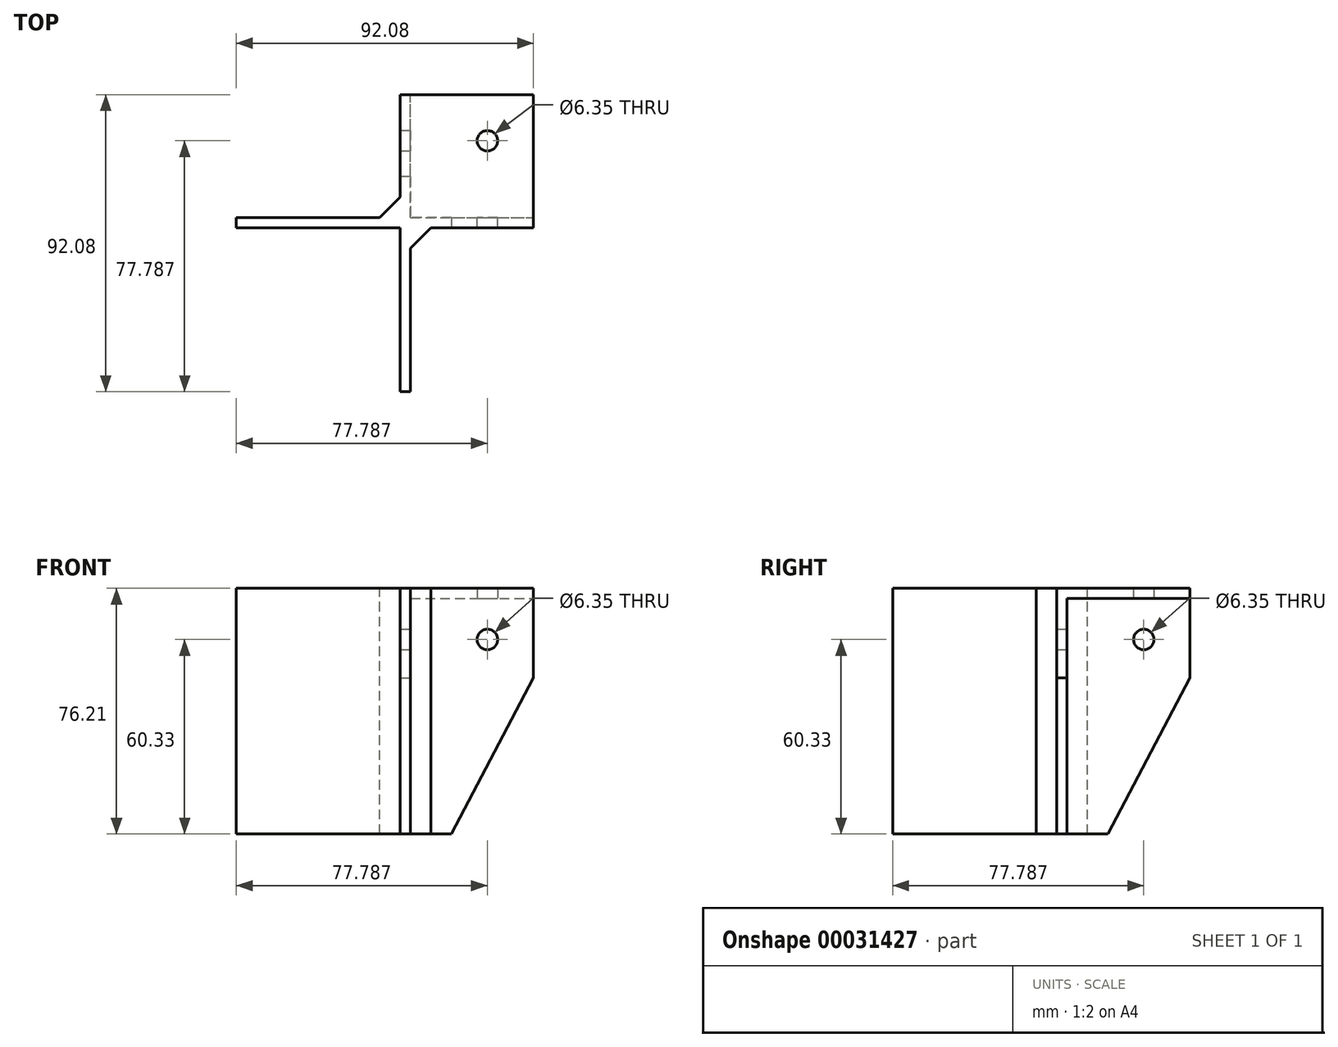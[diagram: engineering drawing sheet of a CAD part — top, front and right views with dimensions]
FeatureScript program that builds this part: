
annotation { "Feature Type Name" : "Feature", "Feature Type Description" : "" }
export const myFeature = defineFeature(function(context is Context, id is Id, definition is map)
    precondition{}
    {
        {
            var Q0;
            Q0=qCreatedBy(makeId("Top.planeOp"),FACE);
            var sketch = newSketch(context, id + "F0", { "sketchPlane" : qUnion([Q0])});
            skLineSegment(sketch, "E0.bottom", {"start": v(0, 0) * mm, "end": v(50.8, 0) * mm});
            skLineSegment(sketch, "E0.top", {"start": v(0, 50.8) * mm, "end": v(50.8, 50.8) * mm});
            skLineSegment(sketch, "E0.left", {"start": v(0, 0) * mm, "end": v(0, 50.8) * mm});
            skLineSegment(sketch, "E0.right", {"start": v(50.8, 0) * mm, "end": v(50.8, 50.8) * mm});
            skSolve(sketch);
        }
        {
            var Q0;
            Q0=makeQuery(id+"F0.imprint","IMPRINT",FACE,{"disambiguationData":[TD([[makeQuery(id+"F0.imprint","IMPRINT",EDGE,{"derivedFrom":sQuery(id+"F0.wireOp",EDGE,"E0.bottom")}),1.0]])]});
            extrude(context, id + "F1", {"entities" : qUnion([Q0]), "depth" : 3.17 * mm});
        }
        {
            var Q0;
            Q0=makeQuery(id+"F1.opExtrude","CAP_FACE",FACE,{"disambiguationData":[OSD([sQuery(id+"F0.wireOp",EDGE,"E0.bottom"),sQuery(id+"F0.wireOp",EDGE,"E0.top"),sQuery(id+"F0.wireOp",EDGE,"E0.left"),sQuery(id+"F0.wireOp",EDGE,"E0.right")])],"isStart":false});
            var sketch = newSketch(context, id + "F2", { "sketchPlane" : qUnion([Q0])});
            skLineSegment(sketch, "E1.bottom", {"start": v(50.8, 0) * mm, "end": v(-50.8, 0) * mm});
            skLineSegment(sketch, "E1.top", {"start": v(50.8, 3.18) * mm, "end": v(-50.8, 3.18) * mm});
            skLineSegment(sketch, "E1.left", {"start": v(50.8, 0) * mm, "end": v(50.8, 3.18) * mm});
            skLineSegment(sketch, "E1.right", {"start": v(-50.8, 0) * mm, "end": v(-50.8, 3.18) * mm});
            skSolve(sketch);
        }
        {
            var Q0;
            {var subQ5=sQuery(id+"F2.wireOp",EDGE,"E1.right");Q0=makeQuery(id+"F2.imprint","IMPRINT",FACE,{"disambiguationData":[TD([[makeQuery(id+"F2.imprint","IMPRINT",EDGE,{"derivedFrom":subQ5}),-1.0]])]});}
            var Q1;
            {var subQ5=sQuery(id+"F2.wireOp",EDGE,"E1.left");Q1=makeQuery(id+"F2.imprint","IMPRINT",FACE,{"disambiguationData":[TD([[makeQuery(id+"F2.imprint","IMPRINT",EDGE,{"derivedFrom":subQ5}),1.0]])]});}
            extrude(context, id + "F3", {"entities" : qUnion([Q0, Q1]), "operationType" : NewBodyOperationType.ADD, "depth" : 12.7 * mm, "hasSecondDirection" : true, "secondDirectionOppositeDirection" : true, "secondDirectionDepth" : 76.2 * mm});
        }
        {
            var Q0;
            Q0=makeQuery(id+"F1.opExtrude","CAP_FACE",FACE,{"disambiguationData":[OSD([sQuery(id+"F0.wireOp",EDGE,"E0.bottom"),sQuery(id+"F0.wireOp",EDGE,"E0.top"),sQuery(id+"F0.wireOp",EDGE,"E0.left"),sQuery(id+"F0.wireOp",EDGE,"E0.right")])],"isStart":false});
            var sketch = newSketch(context, id + "F4", { "sketchPlane" : qUnion([Q0])});
            skLineSegment(sketch, "E2.bottom", {"start": v(0, 50.8) * mm, "end": v(3.18, 50.8) * mm});
            skLineSegment(sketch, "E2.top", {"start": v(0, -50.8) * mm, "end": v(3.18, -50.8) * mm});
            skLineSegment(sketch, "E2.left", {"start": v(0, 50.8) * mm, "end": v(0, -50.8) * mm});
            skLineSegment(sketch, "E2.right", {"start": v(3.18, 50.8) * mm, "end": v(3.18, -50.8) * mm});
            skSolve(sketch);
        }
        {
            var Q0;
            Q0 = qSketchRegion(id + "F4", true);
            extrude(context, id + "F5", {"entities" : qUnion([Q0]), "operationType" : NewBodyOperationType.ADD, "depth" : 12.7 * mm, "hasSecondDirection" : true, "secondDirectionOppositeDirection" : true, "secondDirectionDepth" : 76.2 * mm});
        }
        {
            var Q0;
            Q0=makeQuery(id+"F5.boolean.opBoolean","MERGE",FACE,{"derivedFrom":[makeQuery(id+"F3.opExtrude","CAP_FACE",FACE,{"disambiguationData":[OSD([sQuery(id+"F2.wireOp",EDGE,"E1.bottom"),sQuery(id+"F2.wireOp",EDGE,"E1.top"),sQuery(id+"F2.wireOp",EDGE,"E1.left"),sQuery(id+"F2.wireOp",EDGE,"E1.right")])],"isStart":false}),makeQuery(id+"F5.opExtrude","CAP_FACE",FACE,{"disambiguationData":[OSD([sQuery(id+"F4.wireOp",EDGE,"E2.bottom"),sQuery(id+"F4.wireOp",EDGE,"E2.top"),sQuery(id+"F4.wireOp",EDGE,"E2.left"),sQuery(id+"F4.wireOp",EDGE,"E2.right")])],"isStart":false})]});
            var sketch = newSketch(context, id + "F6", { "sketchPlane" : qUnion([Q0])});
            skLineSegment(sketch, "E3.0", {"start": v(3.18, 50.8) * mm, "end": v(3.18, 3.18) * mm});
            skLineSegment(sketch, "E3.1", {"start": v(0, 50.8) * mm, "end": v(3.18, 50.8) * mm});
            skLineSegment(sketch, "E3.2", {"start": v(0, 50.8) * mm, "end": v(0, 3.18) * mm});
            skLineSegment(sketch, "E3.3", {"start": v(50.8, 3.18) * mm, "end": v(3.18, 3.18) * mm});
            skLineSegment(sketch, "E3.4", {"start": v(50.8, 0) * mm, "end": v(3.18, 0) * mm});
            skLineSegment(sketch, "E3.5", {"start": v(50.8, 0) * mm, "end": v(50.8, 3.18) * mm});
            skLineSegment(sketch, "E4", {"start": v(3.18, 0) * mm, "end": v(0, 0) * mm});
            skLineSegment(sketch, "E5", {"start": v(0, 0) * mm, "end": v(0, 3.18) * mm});
            skSolve(sketch);
        }
        {
            var Q0;
            {var subQ0=sQuery(id+"F4.wireOp",EDGE,"E2.right");var subQ3=sQuery(id+"F0.wireOp",EDGE,"E0.top");Q0=makeQuery(id+"F5.boolean.opBoolean","SPLIT",FACE,{"disambiguationData":[TD([makeQuery(id+"F1.opExtrude","CAP_FACE",FACE,{"disambiguationData":[OSD([sQuery(id+"F0.wireOp",EDGE,"E0.bottom"),subQ3,sQuery(id+"F0.wireOp",EDGE,"E0.left"),sQuery(id+"F0.wireOp",EDGE,"E0.right")])],"isStart":false})])],"derivedFrom":makeQuery(id+"F5.opExtrude","SWEPT_FACE",FACE,{"disambiguationData":[OSD([subQ0])]})});}
            var sketch = newSketch(context, id + "F7", { "sketchPlane" : qUnion([Q0])});
            skLineSegment(sketch, "E6.0", {"start": v(50.8, 15.88) * mm, "end": v(50.8, 3.18) * mm});
            skLineSegment(sketch, "E6.1", {"start": v(3.18, 3.18) * mm, "end": v(50.8, 3.18) * mm});
            skLineSegment(sketch, "E6.2", {"start": v(50.8, 15.88) * mm, "end": v(3.18, 15.88) * mm});
            skLineSegment(sketch, "E6.3", {"start": v(3.18, 3.18) * mm, "end": v(3.18, 15.88) * mm});
            skSolve(sketch);
        }
        {
            var Q0;
            Q0=makeQuery(id+"F7.imprint","IMPRINT",FACE,{"disambiguationData":[TD([[makeQuery(id+"F7.imprint","IMPRINT",EDGE,{"derivedFrom":sQuery(id+"F7.wireOp",EDGE,"E6.0")}),-1.0]])]});
            extrude(context, id + "F8", {"entities" : qUnion([Q0]), "operationType" : NewBodyOperationType.REMOVE, "oppositeDirection" : true, "depth" : 25.4 * mm});
        }
        {
            var Q0;
            {var subQ0=sQuery(id+"F2.wireOp",EDGE,"E1.top");var subQ1=makeQuery(id+"F3.opExtrude","SWEPT_FACE",FACE,{"disambiguationData":[OSD([subQ0])]});var subQ11=sQuery(id+"F0.wireOp",EDGE,"E0.left");var subQ12=sQuery(id+"F0.wireOp",EDGE,"E0.right");Q0=makeQuery(id+"F8.boolean.opBoolean","MERGE",FACE,{"derivedFrom":[makeQuery(id+"F5.boolean.opBoolean","SPLIT",FACE,{"disambiguationData":[TD([makeQuery(id+"F1.opExtrude","SWEPT_FACE",FACE,{"disambiguationData":[OSD([subQ11])]})])],"derivedFrom":subQ1}),makeQuery(id+"F5.boolean.opBoolean","SPLIT",FACE,{"disambiguationData":[TD([makeQuery(id+"F1.opExtrude","CAP_FACE",FACE,{"disambiguationData":[OSD([sQuery(id+"F0.wireOp",EDGE,"E0.bottom"),sQuery(id+"F0.wireOp",EDGE,"E0.top"),subQ11,subQ12])],"isStart":false})])],"derivedFrom":subQ1}),makeQuery(id+"F8.opExtrude","SWEPT_FACE",FACE,{"disambiguationData":[OSD([sQuery(id+"F7.wireOp",EDGE,"E6.3")])]})]});}
            var sketch = newSketch(context, id + "F9", { "sketchPlane" : qUnion([Q0])});
            skLineSegment(sketch, "E7.0", {"start": v(-50.8, 15.88) * mm, "end": v(-3.18, 15.88) * mm});
            skLineSegment(sketch, "E7.1", {"start": v(-3.18, 3.18) * mm, "end": v(-50.8, 3.18) * mm});
            skLineSegment(sketch, "E7.2", {"start": v(-50.8, 15.88) * mm, "end": v(-50.8, 3.18) * mm});
            skLineSegment(sketch, "E8", {"start": v(-3.18, 15.88) * mm, "end": v(-3.18, 3.18) * mm});
            skPoint(sketch, "E9.orphan", {"position": v(0, 3.18) * mm});
            skSolve(sketch);
        }
        {
            var Q0;
            Q0=makeQuery(id+"F9.imprint","IMPRINT",FACE,{"disambiguationData":[TD([[makeQuery(id+"F9.imprint","IMPRINT",EDGE,{"derivedFrom":sQuery(id+"F9.wireOp",EDGE,"E7.0")}),-1.0]])]});
            extrude(context, id + "F10", {"entities" : qUnion([Q0]), "operationType" : NewBodyOperationType.REMOVE, "oppositeDirection" : true, "depth" : 25.4 * mm});
        }
        {
            var Q0;
            {var subQ0=sQuery(id+"F2.wireOp",EDGE,"E1.bottom");Q0=makeQuery(id+"F5.boolean.opBoolean","SPLIT",FACE,{"disambiguationData":[TD([makeQuery(id+"F1.opExtrude","SWEPT_FACE",FACE,{"disambiguationData":[OSD([sQuery(id+"F0.wireOp",EDGE,"E0.right")])]})])],"derivedFrom":makeQuery(id+"F3.boolean.opBoolean","MERGE",FACE,{"derivedFrom":[makeQuery(id+"F1.opExtrude","SWEPT_FACE",FACE,{"disambiguationData":[OSD([sQuery(id+"F0.wireOp",EDGE,"E0.bottom")])]}),makeQuery(id+"F3.opExtrude","SWEPT_FACE",FACE,{"disambiguationData":[OSD([subQ0])]})]})});}
            var sketch = newSketch(context, id + "F11", { "sketchPlane" : qUnion([Q0])});
            skLineSegment(sketch, "E10", {"start": v(3.18, -73.03) * mm, "end": v(15.88, -73.03) * mm, "construction": true});
            skLineSegment(sketch, "E11", {"start": v(50.8, 0) * mm, "end": v(50.8, -6.35) * mm, "construction": true});
            skLineSegment(sketch, "E12", {"start": v(15.88, -73.03) * mm, "end": v(50.8, -6.35) * mm});
            skLineSegment(sketch, "E13", {"start": v(50.8, -6.35) * mm, "end": v(50.8, -73.03) * mm});
            skLineSegment(sketch, "E14", {"start": v(50.8, -73.03) * mm, "end": v(15.88, -73.03) * mm});
            skSolve(sketch);
        }
        {
            var Q0;
            Q0=makeQuery(id+"F11.imprint","IMPRINT",FACE,{"disambiguationData":[TD([[makeQuery(id+"F11.imprint","IMPRINT",EDGE,{"derivedFrom":sQuery(id+"F11.wireOp",EDGE,"E12")}),-1.0]])]});
            extrude(context, id + "F12", {"entities" : qUnion([Q0]), "operationType" : NewBodyOperationType.REMOVE, "oppositeDirection" : true, "depth" : 25.4 * mm});
        }
        {
            var Q0;
            Q0=makeQuery(id+"F5.boolean.opBoolean","MERGE",FACE,{"derivedFrom":[makeQuery(id+"F1.opExtrude","SWEPT_FACE",FACE,{"disambiguationData":[OSD([sQuery(id+"F0.wireOp",EDGE,"E0.left")])]}),makeQuery(id+"F5.opExtrude","SWEPT_FACE",FACE,{"disambiguationData":[OSD([sQuery(id+"F4.wireOp",EDGE,"E2.left")])]})]});
            var sketch = newSketch(context, id + "F13", { "sketchPlane" : qUnion([Q0])});
            skLineSegment(sketch, "E15", {"start": v(-50.8, 3.18) * mm, "end": v(-50.8, -6.35) * mm, "construction": true});
            skLineSegment(sketch, "E16", {"start": v(-50.8, -6.35) * mm, "end": v(-15.88, -73.03) * mm});
            skLineSegment(sketch, "E17", {"start": v(-15.88, -73.03) * mm, "end": v(-3.18, -73.03) * mm, "construction": true});
            skLineSegment(sketch, "E18", {"start": v(-50.8, -6.35) * mm, "end": v(-50.8, -73.03) * mm});
            skLineSegment(sketch, "E19", {"start": v(-50.8, -73.03) * mm, "end": v(-15.88, -73.03) * mm});
            skSolve(sketch);
        }
        {
            var Q0;
            Q0=makeQuery(id+"F13.imprint","IMPRINT",FACE,{"disambiguationData":[TD([[makeQuery(id+"F13.imprint","IMPRINT",EDGE,{"derivedFrom":sQuery(id+"F13.wireOp",EDGE,"E16")}),-1.0]])]});
            extrude(context, id + "F14", {"entities" : qUnion([Q0]), "operationType" : NewBodyOperationType.REMOVE, "oppositeDirection" : true, "depth" : 25.4 * mm});
        }
        {
            var Q0;
            {var subQ0=sQuery(id+"F2.wireOp",EDGE,"E1.top");var subQ1=makeQuery(id+"F3.opExtrude","SWEPT_FACE",FACE,{"disambiguationData":[OSD([subQ0])]});var subQ11=sQuery(id+"F0.wireOp",EDGE,"E0.left");var subQ12=sQuery(id+"F0.wireOp",EDGE,"E0.right");Q0=makeQuery(id+"F8.boolean.opBoolean","MERGE",FACE,{"derivedFrom":[makeQuery(id+"F5.boolean.opBoolean","SPLIT",FACE,{"disambiguationData":[TD([makeQuery(id+"F1.opExtrude","SWEPT_FACE",FACE,{"disambiguationData":[OSD([subQ11])]})])],"derivedFrom":subQ1}),makeQuery(id+"F5.boolean.opBoolean","SPLIT",FACE,{"disambiguationData":[TD([makeQuery(id+"F1.opExtrude","CAP_FACE",FACE,{"disambiguationData":[OSD([sQuery(id+"F0.wireOp",EDGE,"E0.bottom"),sQuery(id+"F0.wireOp",EDGE,"E0.top"),subQ11,subQ12])],"isStart":false})])],"derivedFrom":subQ1}),makeQuery(id+"F8.opExtrude","SWEPT_FACE",FACE,{"disambiguationData":[OSD([sQuery(id+"F7.wireOp",EDGE,"E6.3")])]})]});}
            var sketch = newSketch(context, id + "F15", { "sketchPlane" : qUnion([Q0])});
            skLineSegment(sketch, "E20.bottom", {"start": v(-3.18, 15.88) * mm, "end": v(50.8, 15.88) * mm});
            skLineSegment(sketch, "E20.top", {"start": v(-3.18, 3.18) * mm, "end": v(50.8, 3.18) * mm});
            skLineSegment(sketch, "E20.left", {"start": v(-3.18, 15.88) * mm, "end": v(-3.18, 3.18) * mm});
            skLineSegment(sketch, "E20.right", {"start": v(50.8, 15.88) * mm, "end": v(50.8, 3.18) * mm});
            skSolve(sketch);
        }
        {
            var Q0;
            Q0=makeQuery(id+"F15.imprint","IMPRINT",FACE,{"disambiguationData":[TD([[makeQuery(id+"F15.imprint","IMPRINT",EDGE,{"derivedFrom":sQuery(id+"F15.wireOp",EDGE,"E20.bottom")}),-1.0]])]});
            extrude(context, id + "F16", {"entities" : qUnion([Q0]), "operationType" : NewBodyOperationType.REMOVE, "endBound" : BoundingType.THROUGH_ALL, "oppositeDirection" : true, "depth" : 25.4 * mm});
        }
        {
            var Q0;
            Q0=makeQuery(id+"F16.boolean.opBoolean","MERGE",FACE,{"derivedFrom":[makeQuery(id+"F10.boolean.opBoolean","MERGE",FACE,{"derivedFrom":[makeQuery(id+"F8.boolean.opBoolean","MERGE",FACE,{"derivedFrom":[makeQuery(id+"F1.opExtrude","CAP_FACE",FACE,{"disambiguationData":[OSD([sQuery(id+"F0.wireOp",EDGE,"E0.bottom"),sQuery(id+"F0.wireOp",EDGE,"E0.top"),sQuery(id+"F0.wireOp",EDGE,"E0.left"),sQuery(id+"F0.wireOp",EDGE,"E0.right")])],"isStart":false}),makeQuery(id+"F8.opExtrude","SWEPT_FACE",FACE,{"disambiguationData":[OSD([sQuery(id+"F7.wireOp",EDGE,"E6.1")])]})]}),makeQuery(id+"F10.opExtrude","SWEPT_FACE",FACE,{"disambiguationData":[OSD([sQuery(id+"F9.wireOp",EDGE,"E7.1")])]})]}),makeQuery(id+"F16.opExtrude","SWEPT_FACE",FACE,{"disambiguationData":[OSD([sQuery(id+"F15.wireOp",EDGE,"E20.top")])]})]});
            var sketch = newSketch(context, id + "F17", { "sketchPlane" : qUnion([Q0])});
            skLineSegment(sketch, "E21", {"start": v(3.18, 0) * mm, "end": v(3.18, -6.35) * mm});
            skLineSegment(sketch, "E22", {"start": v(3.18, -6.35) * mm, "end": v(9.53, 0) * mm});
            skLineSegment(sketch, "E23", {"start": v(9.53, 0) * mm, "end": v(3.18, 0) * mm});
            skLineSegment(sketch, "E24", {"start": v(0, 3.18) * mm, "end": v(0, 9.53) * mm});
            skLineSegment(sketch, "E25", {"start": v(0, 9.53) * mm, "end": v(-6.35, 3.18) * mm});
            skLineSegment(sketch, "E26", {"start": v(-6.35, 3.18) * mm, "end": v(0, 3.18) * mm});
            skSolve(sketch);
        }
        {
            var Q0;
            Q0 = qSketchRegion(id + "F17", true);
            var Q1;
            Q1=makeQuery(id+"F5.boolean.opBoolean","MERGE",FACE,{"derivedFrom":[makeQuery(id+"F3.opExtrude","CAP_FACE",FACE,{"disambiguationData":[OSD([sQuery(id+"F2.wireOp",EDGE,"E1.bottom"),sQuery(id+"F2.wireOp",EDGE,"E1.top"),sQuery(id+"F2.wireOp",EDGE,"E1.left"),sQuery(id+"F2.wireOp",EDGE,"E1.right")])],"isStart":true}),makeQuery(id+"F5.opExtrude","CAP_FACE",FACE,{"disambiguationData":[OSD([sQuery(id+"F4.wireOp",EDGE,"E2.bottom"),sQuery(id+"F4.wireOp",EDGE,"E2.top"),sQuery(id+"F4.wireOp",EDGE,"E2.left"),sQuery(id+"F4.wireOp",EDGE,"E2.right")])],"isStart":true})]});
            extrude(context, id + "F18", {"entities" : qUnion([Q0]), "operationType" : NewBodyOperationType.ADD, "endBound" : BoundingType.UP_TO_SURFACE, "oppositeDirection" : true, "endBoundEntityFace" : qUnion([Q1]), "depth" : 25.4 * mm});
        }
        {
            var Q0;
            {var subQ0=sQuery(id+"F2.wireOp",EDGE,"E1.top");var subQ3=sQuery(id+"F0.wireOp",EDGE,"E0.right");Q0=makeQuery(id+"F5.boolean.opBoolean","SPLIT",FACE,{"disambiguationData":[TD([makeQuery(id+"F1.opExtrude","CAP_FACE",FACE,{"disambiguationData":[OSD([sQuery(id+"F0.wireOp",EDGE,"E0.bottom"),sQuery(id+"F0.wireOp",EDGE,"E0.top"),sQuery(id+"F0.wireOp",EDGE,"E0.left"),subQ3])],"isStart":true})])],"derivedFrom":makeQuery(id+"F3.opExtrude","SWEPT_FACE",FACE,{"disambiguationData":[OSD([subQ0])]})});}
            var sketch = newSketch(context, id + "F19", { "sketchPlane" : qUnion([Q0])});
            skLineSegment(sketch, "E27", {"start": v(-26.99, 0) * mm, "end": v(-26.99, -12.7) * mm, "construction": true});
            skPoint(sketch, "E27.endSnap0", {"position": v(-26.99, 0) * mm});
            skCircle(sketch, "E28", {"center": v(-26.99, -12.7) * mm, "radius": 3.18 * mm});
            skSolve(sketch);
        }
        {
            var Q0;
            Q0 = qSketchRegion(id + "F19", true);
            extrude(context, id + "F20", {"entities" : qUnion([Q0]), "operationType" : NewBodyOperationType.REMOVE, "oppositeDirection" : true, "depth" : 25.4 * mm});
        }
        {
            var Q0;
            {var subQ0=sQuery(id+"F4.wireOp",EDGE,"E2.right");var subQ3=sQuery(id+"F0.wireOp",EDGE,"E0.top");Q0=makeQuery(id+"F5.boolean.opBoolean","SPLIT",FACE,{"disambiguationData":[TD([makeQuery(id+"F1.opExtrude","CAP_FACE",FACE,{"disambiguationData":[OSD([sQuery(id+"F0.wireOp",EDGE,"E0.bottom"),subQ3,sQuery(id+"F0.wireOp",EDGE,"E0.left"),sQuery(id+"F0.wireOp",EDGE,"E0.right")])],"isStart":true})])],"derivedFrom":makeQuery(id+"F5.opExtrude","SWEPT_FACE",FACE,{"disambiguationData":[OSD([subQ0])]})});}
            var sketch = newSketch(context, id + "F21", { "sketchPlane" : qUnion([Q0])});
            skLineSegment(sketch, "E29", {"start": v(26.99, 0) * mm, "end": v(26.99, -12.7) * mm, "construction": true});
            skPoint(sketch, "E29.endSnap0", {"position": v(26.99, 0) * mm});
            skCircle(sketch, "E30", {"center": v(26.99, -12.7) * mm, "radius": 3.18 * mm});
            skSolve(sketch);
        }
        {
            var Q0;
            Q0=makeQuery(id+"F21.imprint","IMPRINT",FACE,{"disambiguationData":[TD([[makeQuery(id+"F21.imprint","IMPRINT",EDGE,{"derivedFrom":sQuery(id+"F21.wireOp",EDGE,"E30")}),1.0]])]});
            extrude(context, id + "F22", {"entities" : qUnion([Q0]), "operationType" : NewBodyOperationType.REMOVE, "oppositeDirection" : true, "depth" : 25.4 * mm});
        }
        {
            var Q0;
            Q0=makeQuery(id+"F1.opExtrude","CAP_FACE",FACE,{"disambiguationData":[OSD([sQuery(id+"F0.wireOp",EDGE,"E0.bottom"),sQuery(id+"F0.wireOp",EDGE,"E0.top"),sQuery(id+"F0.wireOp",EDGE,"E0.left"),sQuery(id+"F0.wireOp",EDGE,"E0.right")])],"isStart":true});
            var sketch = newSketch(context, id + "F23", { "sketchPlane" : qUnion([Q0])});
            skLineSegment(sketch, "E31", {"start": v(3.18, -3.18) * mm, "end": v(50.8, -50.8) * mm, "construction": true});
            skLineSegment(sketch, "E32", {"start": v(50.8, -50.8) * mm, "end": v(50.8, -3.18) * mm, "construction": true});
            skLineSegment(sketch, "E33", {"start": v(50.8, -3.18) * mm, "end": v(3.17, -50.8) * mm, "construction": true});
            skCircle(sketch, "E34", {"center": v(26.99, -26.99) * mm, "radius": 3.18 * mm});
            skPoint(sketch, "E34.centerSnap0", {"position": v(26.99, -26.99) * mm});
            skSolve(sketch);
        }
        {
            var Q0;
            Q0=makeQuery(id+"F23.imprint","IMPRINT",FACE,{"disambiguationData":[TD([[makeQuery(id+"F23.imprint","IMPRINT",EDGE,{"derivedFrom":sQuery(id+"F23.wireOp",EDGE,"E34")}),1.0]])]});
            var Q1;
            Q1=sQuery(id+"F23.wireOp",EDGE,"E34");
            extrude(context, id + "F24", {"entities" : qUnion([Q0]), "operationType" : NewBodyOperationType.REMOVE, "surfaceEntities" : qUnion([Q1]), "oppositeDirection" : true, "depth" : 25.4 * mm});
        }
        {
            var Q0;
            Q0=makeQuery(id+"F18.boolean.opBoolean","MERGE",FACE,{"derivedFrom":[makeQuery(id+"F16.boolean.opBoolean","MERGE",FACE,{"derivedFrom":[makeQuery(id+"F10.boolean.opBoolean","MERGE",FACE,{"derivedFrom":[makeQuery(id+"F8.boolean.opBoolean","MERGE",FACE,{"derivedFrom":[makeQuery(id+"F1.opExtrude","CAP_FACE",FACE,{"disambiguationData":[OSD([sQuery(id+"F0.wireOp",EDGE,"E0.bottom"),sQuery(id+"F0.wireOp",EDGE,"E0.top"),sQuery(id+"F0.wireOp",EDGE,"E0.left"),sQuery(id+"F0.wireOp",EDGE,"E0.right")])],"isStart":false}),makeQuery(id+"F8.opExtrude","SWEPT_FACE",FACE,{"disambiguationData":[OSD([sQuery(id+"F7.wireOp",EDGE,"E6.1")])]})]}),makeQuery(id+"F10.opExtrude","SWEPT_FACE",FACE,{"disambiguationData":[OSD([sQuery(id+"F9.wireOp",EDGE,"E7.1")])]})]}),makeQuery(id+"F16.opExtrude","SWEPT_FACE",FACE,{"disambiguationData":[OSD([sQuery(id+"F15.wireOp",EDGE,"E20.top")])]})]}),makeQuery(id+"F18.opExtrude","CAP_FACE",FACE,{"disambiguationData":[OSD([sQuery(id+"F17.wireOp",EDGE,"E21"),sQuery(id+"F17.wireOp",EDGE,"E22"),sQuery(id+"F17.wireOp",EDGE,"E23")])],"isStart":true}),makeQuery(id+"F18.opExtrude","CAP_FACE",FACE,{"disambiguationData":[OSD([sQuery(id+"F17.wireOp",EDGE,"E24"),sQuery(id+"F17.wireOp",EDGE,"E25"),sQuery(id+"F17.wireOp",EDGE,"E26")])],"isStart":true})]});
            var sketch = newSketch(context, id + "F25", { "sketchPlane" : qUnion([Q0])});
            skLineSegment(sketch, "E35.bottom", {"start": v(50.8, 0) * mm, "end": v(41.28, 0) * mm});
            skLineSegment(sketch, "E35.top", {"start": v(50.8, 50.8) * mm, "end": v(41.27, 50.8) * mm});
            skLineSegment(sketch, "E35.left", {"start": v(50.8, 0) * mm, "end": v(50.8, 50.8) * mm});
            skLineSegment(sketch, "E35.right", {"start": v(41.28, 0) * mm, "end": v(41.27, 41.28) * mm});
            skLineSegment(sketch, "E36.bottom", {"start": v(41.27, 50.8) * mm, "end": v(0, 50.8) * mm});
            skLineSegment(sketch, "E36.top", {"start": v(41.27, 41.28) * mm, "end": v(0, 41.28) * mm});
            skLineSegment(sketch, "E36.right", {"start": v(0, 50.8) * mm, "end": v(0, 41.28) * mm});
            skSolve(sketch);
        }
        {
            var Q0;
            Q0=makeQuery(id+"F25.imprint","IMPRINT",FACE,{"disambiguationData":[TD([[makeQuery(id+"F25.imprint","IMPRINT",EDGE,{"derivedFrom":sQuery(id+"F25.wireOp",EDGE,"E35.bottom")}),1.0]])]});
            extrude(context, id + "F26", {"entities" : qUnion([Q0]), "operationType" : NewBodyOperationType.REMOVE, "endBound" : BoundingType.THROUGH_ALL, "oppositeDirection" : true, "depth" : 25.4 * mm});
        }
    });
